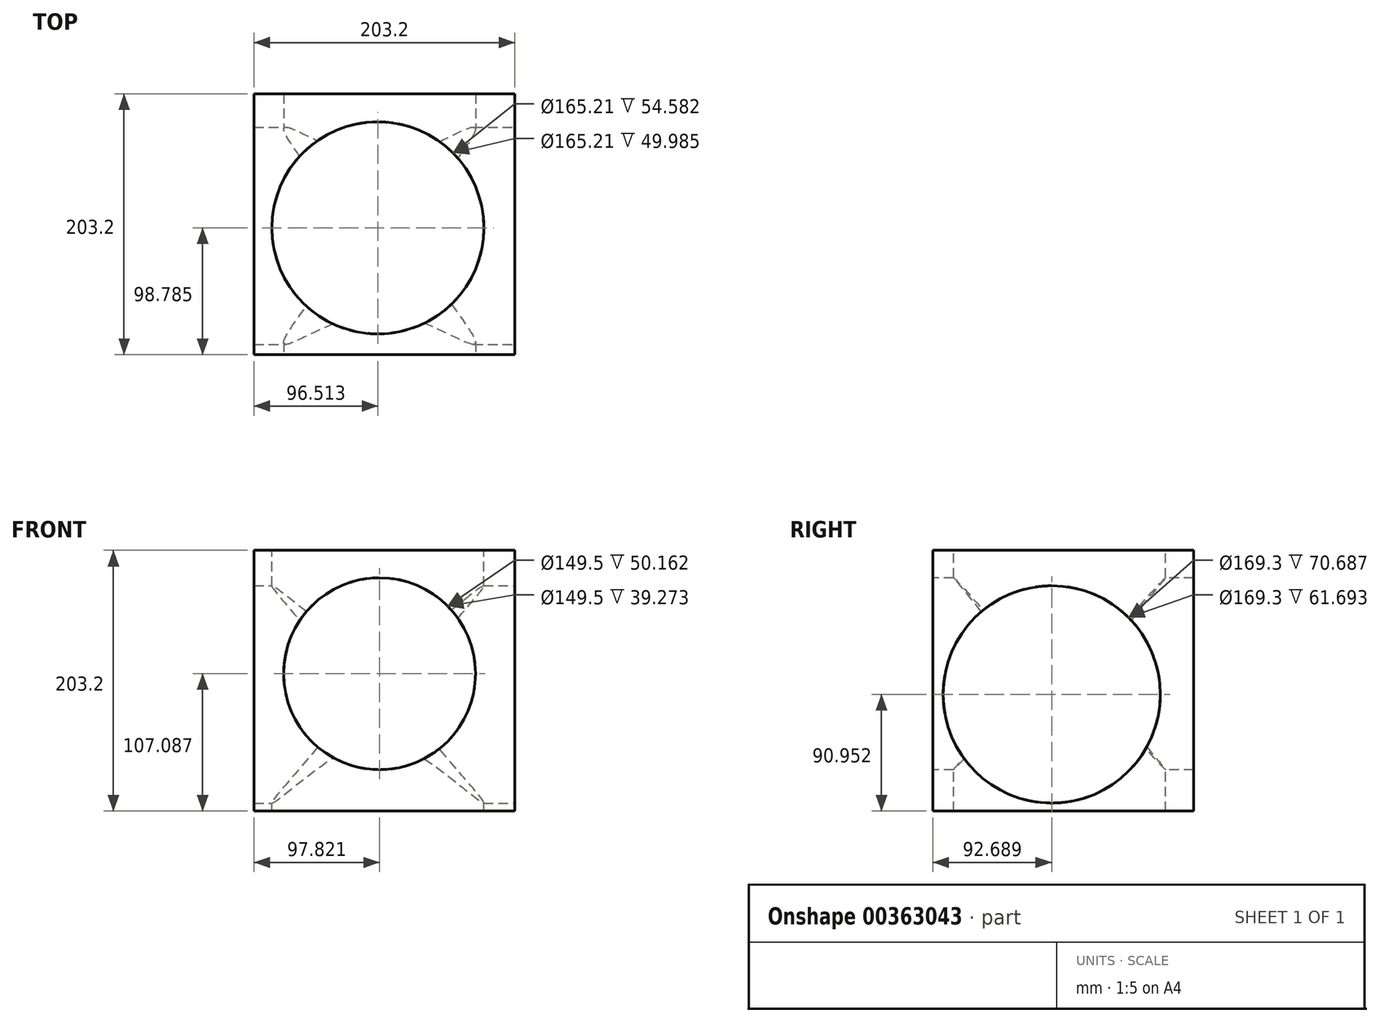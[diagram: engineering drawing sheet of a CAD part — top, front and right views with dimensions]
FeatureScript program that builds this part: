
annotation { "Feature Type Name" : "Feature", "Feature Type Description" : "" }
export const myFeature = defineFeature(function(context is Context, id is Id, definition is map)
    precondition{}
    {
        {
            var Q0;
            Q0=qCreatedBy(makeId("Front.planeOp"),FACE);
            var sketch = newSketch(context, id + "F0", { "sketchPlane" : qUnion([Q0])});
            skLineSegment(sketch, "E0.bottom", {"start": v(0, 0) * mm, "end": v(203.2, 0) * mm});
            skLineSegment(sketch, "E0.top", {"start": v(0, 203.2) * mm, "end": v(203.2, 203.2) * mm});
            skLineSegment(sketch, "E0.left", {"start": v(0, 0) * mm, "end": v(0, 203.2) * mm});
            skLineSegment(sketch, "E0.right", {"start": v(203.2, 0) * mm, "end": v(203.2, 203.2) * mm});
            skSolve(sketch);
        }
        {
            var Q0;
            Q0=makeQuery(id+"F0.imprint","IMPRINT",FACE,{"disambiguationData":[TD([[makeQuery(id+"F0.imprint","IMPRINT",EDGE,{"derivedFrom":sQuery(id+"F0.wireOp",EDGE,"E0.bottom")}),1.0]])]});
            extrude(context, id + "F1", {"entities" : qUnion([Q0]), "depth" : 203.2 * mm});
        }
        {
            var Q0;
            Q0=makeQuery(id+"F1.opExtrude","CAP_FACE",FACE,{"disambiguationData":[OSD([sQuery(id+"F0.wireOp",EDGE,"E0.bottom"),sQuery(id+"F0.wireOp",EDGE,"E0.top"),sQuery(id+"F0.wireOp",EDGE,"E0.left"),sQuery(id+"F0.wireOp",EDGE,"E0.right")])],"isStart":false});
            var sketch = newSketch(context, id + "F2", { "sketchPlane" : qUnion([Q0])});
            skCircle(sketch, "E1", {"center": v(97.82, 107.09) * mm, "radius": 74.75 * mm});
            skSolve(sketch);
        }
        {
            var Q0;
            Q0 = qSketchRegion(id + "F2", true);
            extrude(context, id + "F3", {"entities" : qUnion([Q0]), "operationType" : NewBodyOperationType.REMOVE, "endBound" : BoundingType.THROUGH_ALL, "oppositeDirection" : true, "depth" : 25.4 * mm});
        }
        {
            var Q0;
            Q0=makeQuery(id+"F1.opExtrude","SWEPT_FACE",FACE,{"disambiguationData":[OSD([sQuery(id+"F0.wireOp",EDGE,"E0.top")])]});
            var sketch = newSketch(context, id + "F4", { "sketchPlane" : qUnion([Q0])});
            skCircle(sketch, "E2", {"center": v(96.51, -104.41) * mm, "radius": 82.6 * mm});
            skSolve(sketch);
        }
        {
            var Q0;
            Q0=makeQuery(id+"F4.imprint","IMPRINT",FACE,{"disambiguationData":[TD([[makeQuery(id+"F4.imprint","IMPRINT",EDGE,{"derivedFrom":sQuery(id+"F4.wireOp",EDGE,"E2")}),1.0]])]});
            extrude(context, id + "F5", {"entities" : qUnion([Q0]), "operationType" : NewBodyOperationType.REMOVE, "endBound" : BoundingType.THROUGH_ALL, "oppositeDirection" : true, "depth" : 25.4 * mm});
        }
        {
            var Q0;
            Q0=makeQuery(id+"F1.opExtrude","SWEPT_FACE",FACE,{"disambiguationData":[OSD([sQuery(id+"F0.wireOp",EDGE,"E0.right")])]});
            var sketch = newSketch(context, id + "F6", { "sketchPlane" : qUnion([Q0])});
            skCircle(sketch, "E3", {"center": v(-110.51, 90.95) * mm, "radius": 84.65 * mm});
            skSolve(sketch);
        }
        {
            var Q0;
            Q0 = qSketchRegion(id + "F6", true);
            extrude(context, id + "F7", {"entities" : qUnion([Q0]), "operationType" : NewBodyOperationType.REMOVE, "endBound" : BoundingType.THROUGH_ALL, "oppositeDirection" : true, "depth" : 25.4 * mm});
        }
    });
